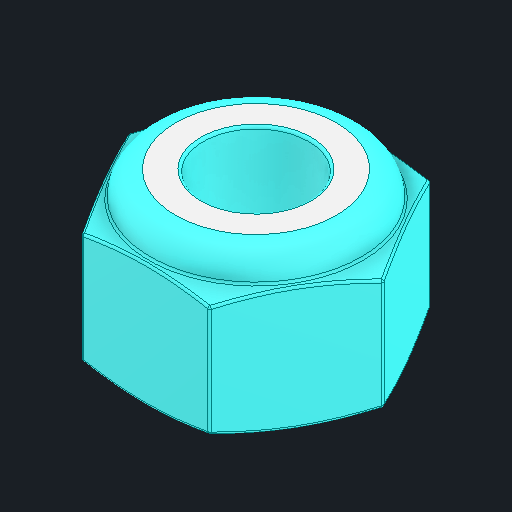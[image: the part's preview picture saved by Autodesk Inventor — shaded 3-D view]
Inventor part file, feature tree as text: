
AUTODESK INVENTOR PART (.ipt)
format: ipt  version: 2025 (Build 290162000, 162)  size: 212,480 bytes
history: native  units: in
note: dims shown in document units (in); Inventor stores cm internally (conversion verified against a paired STEP export)
features: fillet x1
ambient origin geometry x8: Origin, YZ Plane, XZ Plane, XY Plane, X Axis, Y Axis, Z Axis, Center Point
bodies: Solid1 (feature_tree)
feature tree (1):
  fillet  "Fillet2"  [1 undecoded]
note: 1 required parameter value undecoded (feature->parameter linkage not recoverable at this tier; creation-order binding heuristic only, values carry confidence <= 0.55)
